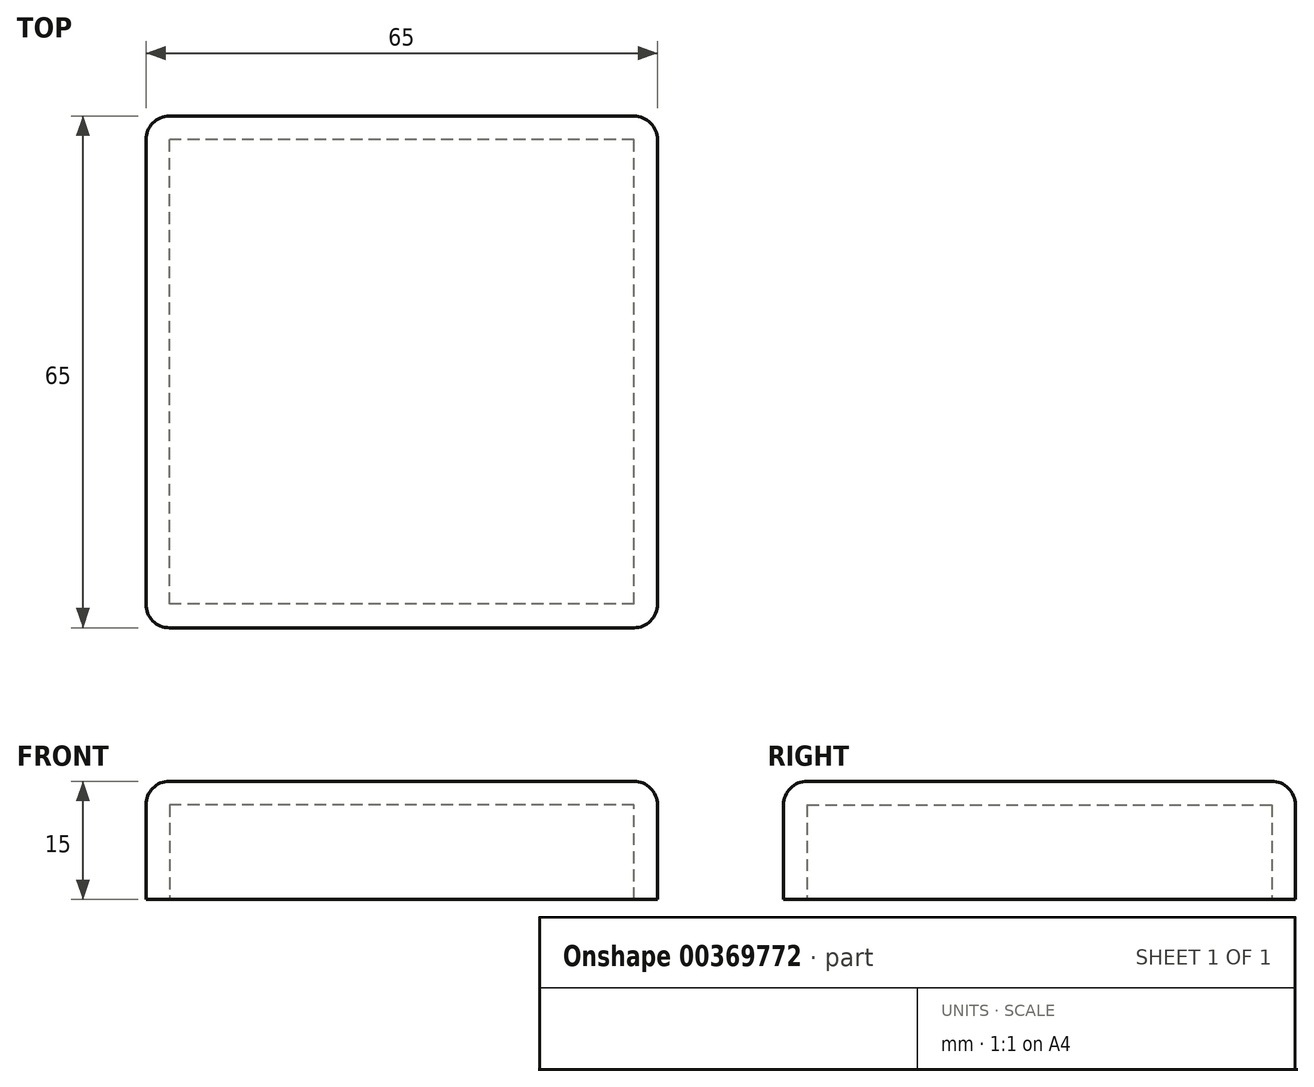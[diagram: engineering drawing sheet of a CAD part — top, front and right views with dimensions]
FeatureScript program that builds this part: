
annotation { "Feature Type Name" : "Feature", "Feature Type Description" : "" }
export const myFeature = defineFeature(function(context is Context, id is Id, definition is map)
    precondition{}
    {
        {
            var Q0;
            Q0=qCreatedBy(makeId("Top.planeOp"),FACE);
            var sketch = newSketch(context, id + "F0", { "sketchPlane" : qUnion([Q0])});
            skLineSegment(sketch, "E0.bottom", {"start": v(32.5, -32.5) * mm, "end": v(-32.5, -32.5) * mm});
            skLineSegment(sketch, "E0.top", {"start": v(32.5, 32.5) * mm, "end": v(-32.5, 32.5) * mm});
            skLineSegment(sketch, "E0.left", {"start": v(32.5, -32.5) * mm, "end": v(32.5, 32.5) * mm});
            skLineSegment(sketch, "E0.right", {"start": v(-32.5, -32.5) * mm, "end": v(-32.5, 32.5) * mm});
            skPoint(sketch, "E0.middle", {"position": v(0, 0) * mm});
            skSolve(sketch);
        }
        {
            var Q0;
            Q0=makeQuery(id+"F0.imprint","IMPRINT",FACE,{"disambiguationData":[TD([[makeQuery(id+"F0.imprint","IMPRINT",EDGE,{"derivedFrom":sQuery(id+"F0.wireOp",EDGE,"E0.bottom")}),-1.0]])]});
            extrude(context, id + "F1", {"entities" : qUnion([Q0]), "depth" : 15 * mm, "offsetDistance" : 25 * mm});
        }
        {
            var Q0;
            Q0=makeQuery(id+"F1.opExtrude","CAP_FACE",FACE,{"disambiguationData":[OSD([sQuery(id+"F0.wireOp",EDGE,"E0.bottom"),sQuery(id+"F0.wireOp",EDGE,"E0.top"),sQuery(id+"F0.wireOp",EDGE,"E0.left"),sQuery(id+"F0.wireOp",EDGE,"E0.right")])],"isStart":false});
            var Q1;
            Q1=makeQuery(id+"F1.opExtrude","SWEPT_EDGE",EDGE,{"disambiguationData":[OSD([sQuery(id+"F0.wireOp",EDGE,"E0.top"),sQuery(id+"F0.wireOp",EDGE,"E0.right")])]});
            var Q2;
            Q2=makeQuery(id+"F1.opExtrude","SWEPT_EDGE",EDGE,{"disambiguationData":[OSD([sQuery(id+"F0.wireOp",EDGE,"E0.bottom"),sQuery(id+"F0.wireOp",EDGE,"E0.right")])]});
            var Q3;
            Q3=makeQuery(id+"F1.opExtrude","SWEPT_EDGE",EDGE,{"disambiguationData":[OSD([sQuery(id+"F0.wireOp",EDGE,"E0.top"),sQuery(id+"F0.wireOp",EDGE,"E0.left")])]});
            var Q4;
            Q4=makeQuery(id+"F1.opExtrude","SWEPT_EDGE",EDGE,{"disambiguationData":[OSD([sQuery(id+"F0.wireOp",EDGE,"E0.bottom"),sQuery(id+"F0.wireOp",EDGE,"E0.left")])]});
            fillet(context, id + "F2", {"entities" : qUnion([Q0, Q1, Q2, Q3, Q4]), "radius" : 3 * mm, "tangentPropagation" : true, "allowEdgeOverflow" : false});
        }
        {
            var Q0;
            Q0=makeQuery(id+"F1.opExtrude","CAP_FACE",FACE,{"disambiguationData":[OSD([sQuery(id+"F0.wireOp",EDGE,"E0.bottom"),sQuery(id+"F0.wireOp",EDGE,"E0.top"),sQuery(id+"F0.wireOp",EDGE,"E0.left"),sQuery(id+"F0.wireOp",EDGE,"E0.right")])],"isStart":true});
            shell(context, id + "F3", {"entities" : qUnion([Q0]), "thickness" : 3 * mm});
        }
    });
